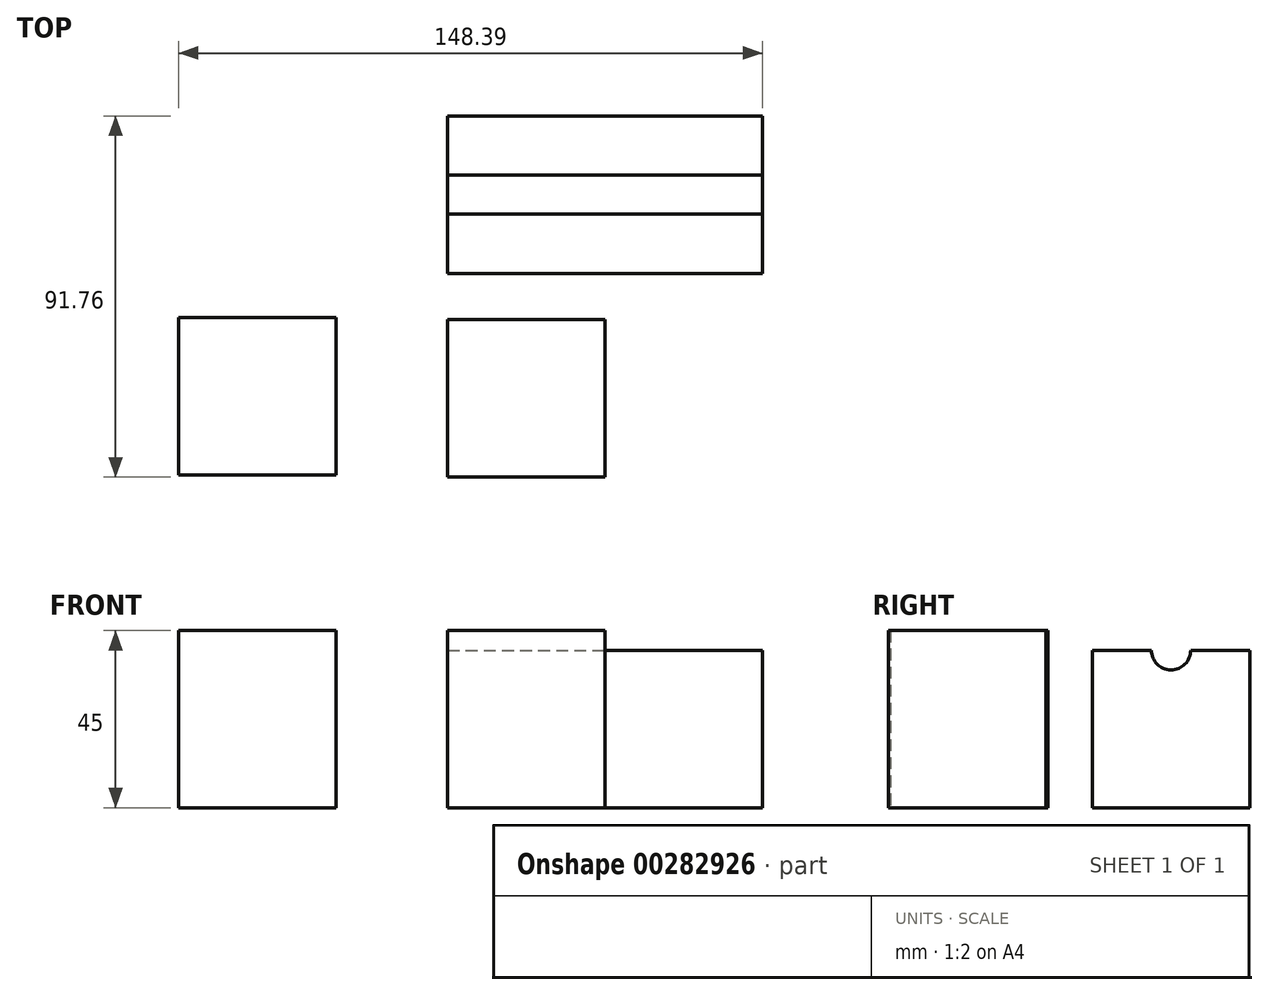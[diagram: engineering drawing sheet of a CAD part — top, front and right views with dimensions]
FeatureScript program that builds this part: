
annotation { "Feature Type Name" : "Feature", "Feature Type Description" : "" }
export const myFeature = defineFeature(function(context is Context, id is Id, definition is map)
    precondition{}
    {
        {
            var Q0;
            Q0=qCreatedBy(makeId("Top.planeOp"),FACE);
            var sketch = newSketch(context, id + "F0", { "sketchPlane" : qUnion([Q0])});
            skLineSegment(sketch, "E0.bottom", {"start": v(0, 0) * mm, "end": v(80, 0) * mm});
            skLineSegment(sketch, "E0.top", {"start": v(0, 40) * mm, "end": v(80, 40) * mm});
            skLineSegment(sketch, "E0.left", {"start": v(0, 0) * mm, "end": v(0, 40) * mm});
            skLineSegment(sketch, "E0.right", {"start": v(80, 0) * mm, "end": v(80, 40) * mm});
            skSolve(sketch);
        }
        {
            var Q0;
            Q0 = qSketchRegion(id + "F0", true);
            extrude(context, id + "F1", {"entities" : qUnion([Q0]), "depth" : 40 * mm, "offsetDistance" : 25 * mm});
        }
        {
            var Q0;
            Q0=makeQuery(id+"F1.opExtrude","SWEPT_FACE",FACE,{"disambiguationData":[OSD([sQuery(id+"F0.wireOp",EDGE,"E0.right")])]});
            var sketch = newSketch(context, id + "F2", { "sketchPlane" : qUnion([Q0])});
            skLineSegment(sketch, "E1", {"start": v(0, 40) * mm, "end": v(20, 40) * mm, "construction": true});
            skCircle(sketch, "E2", {"center": v(20, 40) * mm, "radius": 5 * mm});
            skSolve(sketch);
        }
        {
            var Q0;
            Q0 = qSketchRegion(id + "F2", true);
            extrude(context, id + "F3", {"entities" : qUnion([Q0]), "operationType" : NewBodyOperationType.REMOVE, "oppositeDirection" : true, "depth" : 80 * mm, "offsetDistance" : 25 * mm});
        }
        {
            var Q0;
            Q0=qCreatedBy(makeId("Top.planeOp"),FACE);
            var sketch = newSketch(context, id + "F4", { "sketchPlane" : qUnion([Q0])});
            skLineSegment(sketch, "E3.bottom", {"start": v(0, -11.76) * mm, "end": v(40, -11.76) * mm});
            skLineSegment(sketch, "E3.top", {"start": v(0, -51.76) * mm, "end": v(40, -51.76) * mm});
            skLineSegment(sketch, "E3.left", {"start": v(0, -11.76) * mm, "end": v(0, -51.76) * mm});
            skLineSegment(sketch, "E3.right", {"start": v(40, -11.76) * mm, "end": v(40, -51.76) * mm});
            skLineSegment(sketch, "E4.bottom", {"start": v(-68.39, -11.24) * mm, "end": v(-28.39, -11.24) * mm});
            skLineSegment(sketch, "E4.top", {"start": v(-68.39, -51.24) * mm, "end": v(-28.39, -51.24) * mm});
            skLineSegment(sketch, "E4.left", {"start": v(-68.39, -11.24) * mm, "end": v(-68.39, -51.24) * mm});
            skLineSegment(sketch, "E4.right", {"start": v(-28.39, -11.24) * mm, "end": v(-28.39, -51.24) * mm});
            skSolve(sketch);
        }
        {
            var Q0;
            Q0 = qSketchRegion(id + "F4", true);
            extrude(context, id + "F5", {"entities" : qUnion([Q0]), "depth" : 45 * mm, "offsetDistance" : 25 * mm});
        }
    });
